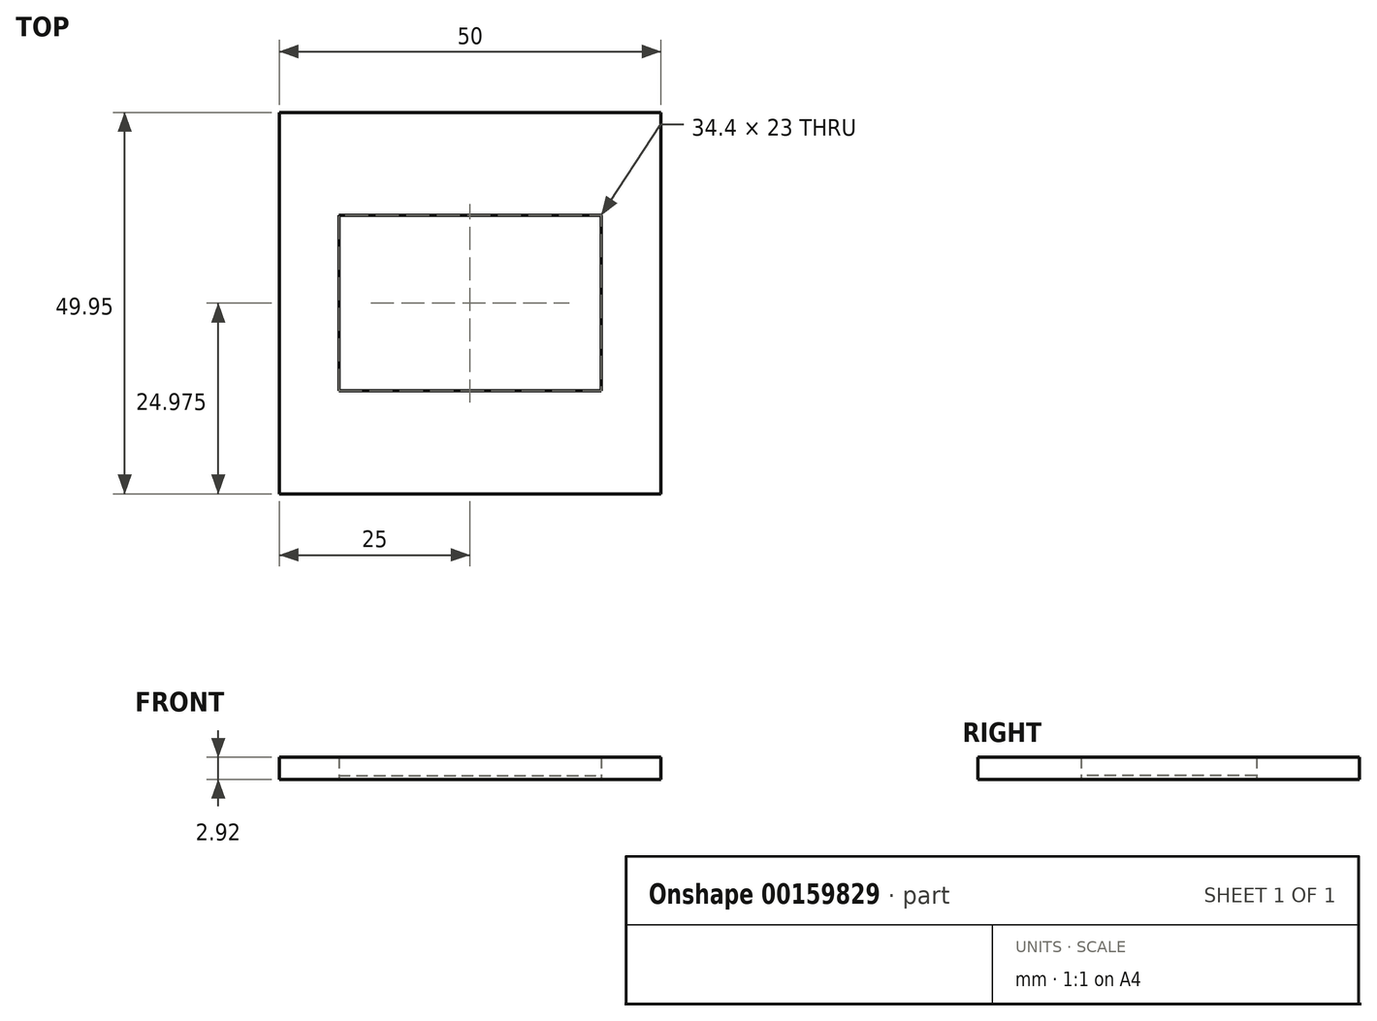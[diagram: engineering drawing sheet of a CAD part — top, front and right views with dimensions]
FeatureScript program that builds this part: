
annotation { "Feature Type Name" : "Feature", "Feature Type Description" : "" }
export const myFeature = defineFeature(function(context is Context, id is Id, definition is map)
    precondition{}
    {
        {
            var Q0;
            Q0=qCreatedBy(makeId("Top.planeOp"),FACE);
            var sketch = newSketch(context, id + "F0", { "sketchPlane" : qUnion([Q0])});
            skLineSegment(sketch, "E0.bottom", {"start": v(0, 0) * mm, "end": v(50, 0) * mm});
            skLineSegment(sketch, "E0.top", {"start": v(0, 49.95) * mm, "end": v(50, 49.95) * mm});
            skLineSegment(sketch, "E0.left", {"start": v(0, 0) * mm, "end": v(0, 49.95) * mm});
            skLineSegment(sketch, "E0.right", {"start": v(50, 0) * mm, "end": v(50, 49.95) * mm});
            skLineSegment(sketch, "E1.bottom", {"start": v(7.8, 36.48) * mm, "end": v(42.2, 36.48) * mm});
            skLineSegment(sketch, "E1.top", {"start": v(7.8, 13.48) * mm, "end": v(42.2, 13.48) * mm});
            skLineSegment(sketch, "E1.left", {"start": v(7.8, 36.48) * mm, "end": v(7.8, 13.48) * mm});
            skLineSegment(sketch, "E1.right", {"start": v(42.2, 36.48) * mm, "end": v(42.2, 13.48) * mm});
            skLineSegment(sketch, "E2", {"start": v(25, 0) * mm, "end": v(25, 13.48) * mm, "construction": true});
            skLineSegment(sketch, "E3", {"start": v(7.8, 24.98) * mm, "end": v(0, 24.98) * mm, "construction": true});
            skSolve(sketch);
        }
        {
            var Q0;
            Q0=qSketchRegion(id+"F0",true);
            extrude(context, id + "F1", {"entities" : qUnion([Q0]), "depth" : 2.92 * mm});
        }
        {
            var Q0;
            Q0=makeQuery(id+"F0.imprint","IMPRINT",FACE,{"disambiguationData":[TD([[makeQuery(id+"F0.imprint","IMPRINT",EDGE,{"derivedFrom":sQuery(id+"F0.wireOp",EDGE,"E1.bottom")}),-1.0]])]});
            extrude(context, id + "F2", {"entities" : qUnion([Q0]), "depth" : .5 * mm});
        }
    });
